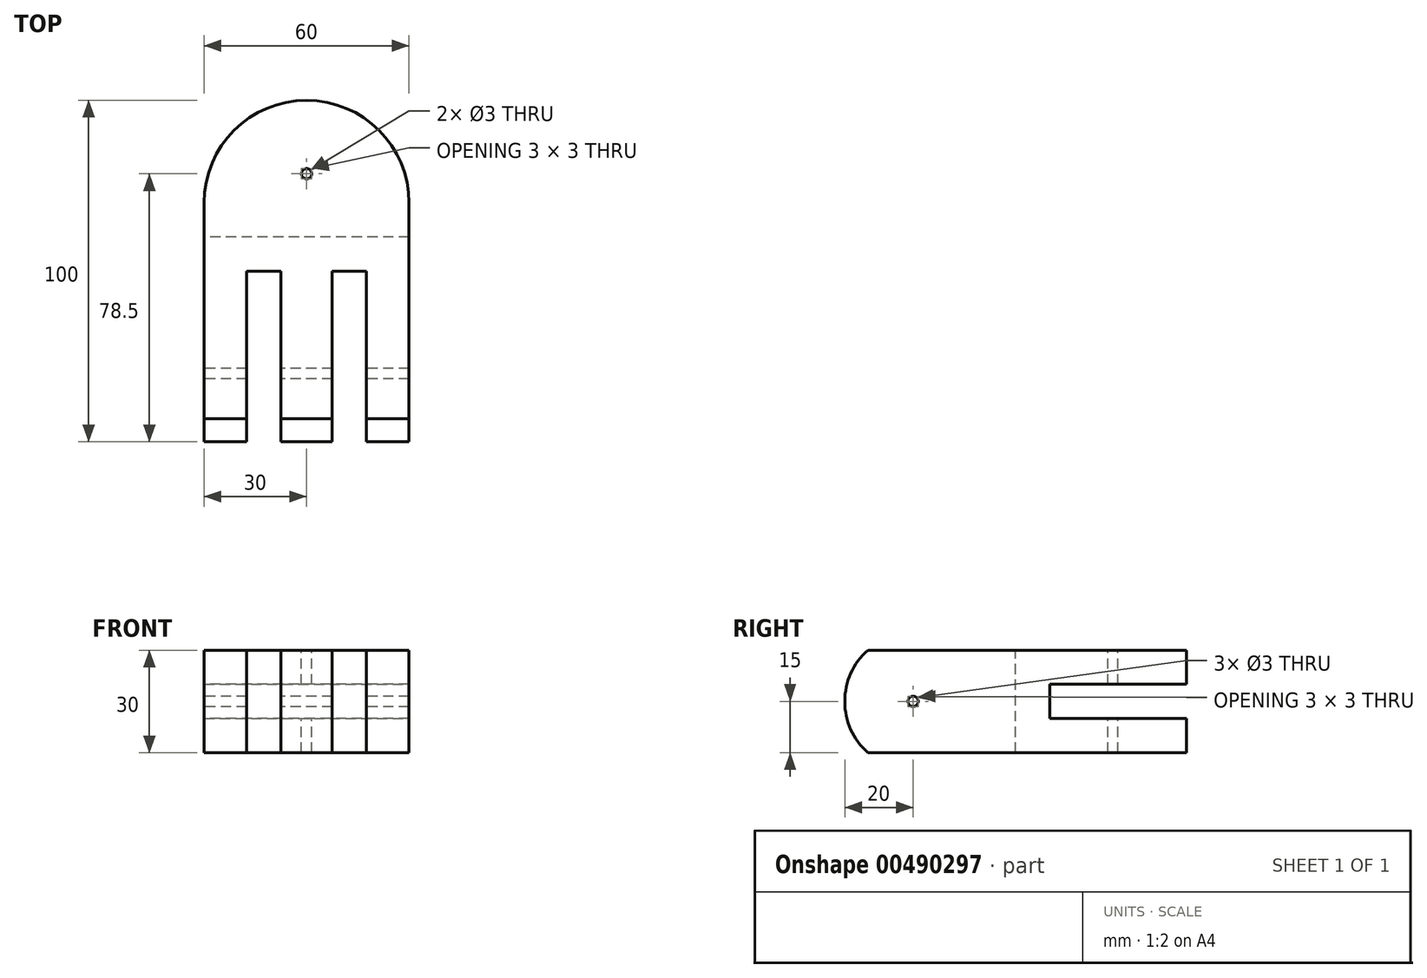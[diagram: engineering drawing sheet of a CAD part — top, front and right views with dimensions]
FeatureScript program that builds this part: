
annotation { "Feature Type Name" : "Feature", "Feature Type Description" : "" }
export const myFeature = defineFeature(function(context is Context, id is Id, definition is map)
    precondition{}
    {
        {
            var Q0;
            Q0=qCreatedBy(makeId("Top.planeOp"),FACE);
            var sketch = newSketch(context, id + "F0", { "sketchPlane" : qUnion([Q0])});
            skLineSegment(sketch, "E0.bottom", {"start": v(30, -50) * mm, "end": v(-30, -50) * mm});
            skLineSegment(sketch, "E0.top", {"start": v(30, 50) * mm, "end": v(-30, 50) * mm});
            skLineSegment(sketch, "E0.left", {"start": v(30, -50) * mm, "end": v(30, 50) * mm});
            skLineSegment(sketch, "E0.right", {"start": v(-30, -50) * mm, "end": v(-30, 50) * mm});
            skPoint(sketch, "E0.middle", {"position": v(0, 0) * mm});
            skSolve(sketch);
        }
        {
            var Q0;
            Q0 = qSketchRegion(id + "F0", true);
            extrude(context, id + "F1", {"entities" : qUnion([Q0]), "depth" : 40 * mm, "offsetDistance" : 25 * mm});
        }
        {
            var Q0;
            Q0=makeQuery(id+"F1.opExtrude","SWEPT_FACE",FACE,{"disambiguationData":[OSD([sQuery(id+"F0.wireOp",EDGE,"E0.top")])]});
            var sketch = newSketch(context, id + "F2", { "sketchPlane" : qUnion([Q0])});
            skLineSegment(sketch, "E1.left", {"start": v(-13, 40) * mm, "end": v(-13, 40) * mm});
            skLineSegment(sketch, "E2.bottom", {"start": v(-30, 25) * mm, "end": v(30, 25) * mm});
            skLineSegment(sketch, "E2.top", {"start": v(-30, 15) * mm, "end": v(30, 15) * mm});
            skLineSegment(sketch, "E2.left", {"start": v(-30, 25) * mm, "end": v(-30, 15) * mm});
            skLineSegment(sketch, "E2.right", {"start": v(30, 25) * mm, "end": v(30, 15) * mm});
            skSolve(sketch);
        }
        {
            var Q0;
            Q0=makeQuery(id+"F2.imprint","IMPRINT",FACE,{"disambiguationData":[TD([[makeQuery(id+"F2.imprint","IMPRINT",EDGE,{"derivedFrom":sQuery(id+"F2.wireOp",EDGE,"E2.bottom")}),-1.0]])]});
            extrude(context, id + "F3", {"entities" : qUnion([Q0]), "operationType" : NewBodyOperationType.REMOVE, "oppositeDirection" : true, "depth" : 40 * mm, "offsetDistance" : 25 * mm});
        }
        {
            var Q0;
            Q0=makeQuery(id+"F1.opExtrude","CAP_FACE",FACE,{"disambiguationData":[OSD([sQuery(id+"F0.wireOp",EDGE,"E0.bottom"),sQuery(id+"F0.wireOp",EDGE,"E0.top"),sQuery(id+"F0.wireOp",EDGE,"E0.left"),sQuery(id+"F0.wireOp",EDGE,"E0.right")])],"isStart":false});
            var sketch = newSketch(context, id + "F4", { "sketchPlane" : qUnion([Q0])});
            skCircle(sketch, "E3", {"center": v(0, 28.5) * mm, "radius": 1.5 * mm});
            skSolve(sketch);
        }
        {
            var Q0;
            Q0=makeQuery(id+"F4.imprint","IMPRINT",FACE,{"disambiguationData":[TD([[makeQuery(id+"F4.imprint","IMPRINT",EDGE,{"derivedFrom":sQuery(id+"F4.wireOp",EDGE,"E3")}),1.0]])]});
            extrude(context, id + "F5", {"entities" : qUnion([Q0]), "operationType" : NewBodyOperationType.REMOVE, "oppositeDirection" : true, "depth" : 88.4 * mm, "offsetDistance" : 25 * mm});
        }
        {
            var Q0;
            Q0=makeQuery(id+"F1.opExtrude","SWEPT_FACE",FACE,{"disambiguationData":[OSD([sQuery(id+"F0.wireOp",EDGE,"E0.right")])]});
            var sketch = newSketch(context, id + "F6", { "sketchPlane" : qUnion([Q0])});
            skCircle(sketch, "E4", {"center": v(30, 20) * mm, "radius": 1.5 * mm});
            skPoint(sketch, "E4.centerSnap0", {"position": v(-10, 20) * mm});
            skSolve(sketch);
        }
        {
            var Q0;
            Q0 = qSketchRegion(id + "F6", true);
            extrude(context, id + "F7", {"entities" : qUnion([Q0]), "operationType" : NewBodyOperationType.REMOVE, "oppositeDirection" : true, "depth" : 101.4 * mm, "offsetDistance" : 25 * mm});
        }
        {
            var Q0;
            Q0=makeQuery(id+"F1.opExtrude","CAP_FACE",FACE,{"disambiguationData":[OSD([sQuery(id+"F0.wireOp",EDGE,"E0.bottom"),sQuery(id+"F0.wireOp",EDGE,"E0.top"),sQuery(id+"F0.wireOp",EDGE,"E0.left"),sQuery(id+"F0.wireOp",EDGE,"E0.right")])],"isStart":false});
            var sketch = newSketch(context, id + "F8", { "sketchPlane" : qUnion([Q0])});
            skLineSegment(sketch, "E5.bottom", {"start": v(-17.5, -50) * mm, "end": v(-7.5, -50) * mm});
            skLineSegment(sketch, "E5.top", {"start": v(-17.5, 0) * mm, "end": v(-7.5, 0) * mm});
            skLineSegment(sketch, "E5.left", {"start": v(-17.5, -50) * mm, "end": v(-17.5, 0) * mm});
            skLineSegment(sketch, "E5.right", {"start": v(-7.5, -50) * mm, "end": v(-7.5, 0) * mm});
            skLineSegment(sketch, "E6.bottom", {"start": v(7.5, 0) * mm, "end": v(17.5, 0) * mm});
            skLineSegment(sketch, "E6.top", {"start": v(7.5, -50) * mm, "end": v(17.5, -50) * mm});
            skLineSegment(sketch, "E6.right", {"start": v(7.5, 0) * mm, "end": v(7.5, -50) * mm});
            skLineSegment(sketch, "E7", {"start": v(17.5, -50) * mm, "end": v(17.5, 0) * mm});
            skSolve(sketch);
        }
        {
            var Q0;
            Q0=makeQuery(id+"F8.imprint","IMPRINT",FACE,{"disambiguationData":[TD([[makeQuery(id+"F8.imprint","IMPRINT",EDGE,{"derivedFrom":sQuery(id+"F8.wireOp",EDGE,"E5.bottom")}),-1.0]])]});
            var Q1;
            Q1=makeQuery(id+"F8.imprint","IMPRINT",FACE,{"disambiguationData":[TD([[makeQuery(id+"F8.imprint","IMPRINT",EDGE,{"derivedFrom":sQuery(id+"F8.wireOp",EDGE,"AMtmPXIM-BORS-Hj5c-r4cM-iqdEoAU15gwC.bottom")}),-1.0]])]});
            var Q2;
            Q2=makeQuery(id+"F8.imprint","IMPRINT",FACE,{"disambiguationData":[TD([[makeQuery(id+"F8.imprint","IMPRINT",EDGE,{"derivedFrom":sQuery(id+"F8.wireOp",EDGE,"E6.bottom")}),-1.0]])]});
            extrude(context, id + "F9", {"entities" : qUnion([Q0, Q1, Q2]), "operationType" : NewBodyOperationType.REMOVE, "oppositeDirection" : true, "depth" : 70.3 * mm, "offsetDistance" : 25 * mm});
        }
        {
            var Q0;
            {var subQ0=sQuery(id+"F0.wireOp",EDGE,"E0.bottom");var subQ1=sQuery(id+"F0.wireOp",EDGE,"E0.right");Q0=makeQuery(id+"F9.boolean.opBoolean","SPLIT",EDGE,{"disambiguationData":[TD([makeQuery(id+"F1.opExtrude","SWEPT_FACE",FACE,{"disambiguationData":[OSD([subQ1])]})])],"derivedFrom":makeQuery(id+"F1.opExtrude","CAP_EDGE",EDGE,{"disambiguationData":[OSD([subQ0])],"isStart":true})});}
            var Q1;
            {var subQ0=sQuery(id+"F0.wireOp",EDGE,"E0.bottom");var subQ1=sQuery(id+"F0.wireOp",EDGE,"E0.right");Q1=makeQuery(id+"F9.boolean.opBoolean","SPLIT",EDGE,{"disambiguationData":[TD([makeQuery(id+"F1.opExtrude","SWEPT_FACE",FACE,{"disambiguationData":[OSD([subQ1])]})])],"derivedFrom":makeQuery(id+"F1.opExtrude","CAP_EDGE",EDGE,{"disambiguationData":[OSD([subQ0])],"isStart":false})});}
            var Q2;
            {var subQ0=sQuery(id+"F0.wireOp",EDGE,"E0.bottom");Q2=makeQuery(id+"F9.boolean.opBoolean","SPLIT",EDGE,{"disambiguationData":[TD([makeQuery(id+"F9.opExtrude","SWEPT_FACE",FACE,{"disambiguationData":[OSD([sQuery(id+"F8.wireOp",EDGE,"E5.right")])]})])],"derivedFrom":makeQuery(id+"F1.opExtrude","CAP_EDGE",EDGE,{"disambiguationData":[OSD([subQ0])],"isStart":false})});}
            var Q3;
            {var subQ0=sQuery(id+"F0.wireOp",EDGE,"E0.bottom");Q3=makeQuery(id+"F9.boolean.opBoolean","SPLIT",EDGE,{"disambiguationData":[TD([makeQuery(id+"F9.opExtrude","SWEPT_FACE",FACE,{"disambiguationData":[OSD([sQuery(id+"F8.wireOp",EDGE,"E5.right")])]})])],"derivedFrom":makeQuery(id+"F1.opExtrude","CAP_EDGE",EDGE,{"disambiguationData":[OSD([subQ0])],"isStart":true})});}
            var Q4;
            {var subQ0=sQuery(id+"F0.wireOp",EDGE,"E0.bottom");var subQ1=sQuery(id+"F0.wireOp",EDGE,"E0.left");Q4=makeQuery(id+"F9.boolean.opBoolean","SPLIT",EDGE,{"disambiguationData":[TD([makeQuery(id+"F1.opExtrude","SWEPT_FACE",FACE,{"disambiguationData":[OSD([subQ1])]})])],"derivedFrom":makeQuery(id+"F1.opExtrude","CAP_EDGE",EDGE,{"disambiguationData":[OSD([subQ0])],"isStart":true})});}
            var Q5;
            {var subQ0=sQuery(id+"F0.wireOp",EDGE,"E0.bottom");var subQ1=sQuery(id+"F0.wireOp",EDGE,"E0.left");Q5=makeQuery(id+"F9.boolean.opBoolean","SPLIT",EDGE,{"disambiguationData":[TD([makeQuery(id+"F1.opExtrude","SWEPT_FACE",FACE,{"disambiguationData":[OSD([subQ1])]})])],"derivedFrom":makeQuery(id+"F1.opExtrude","CAP_EDGE",EDGE,{"disambiguationData":[OSD([subQ0])],"isStart":false})});}
            fillet(context, id + "F10", {"entities" : qUnion([Q0, Q1, Q2, Q3, Q4, Q5]), "radius" : 20 * mm, "tangentPropagation" : true, "allowEdgeOverflow" : false});
        }
        {
            var Q0;
            {var subQ0=sQuery(id+"F0.wireOp",EDGE,"E0.right");var subQ1=sQuery(id+"F0.wireOp",EDGE,"E0.top");Q0=makeQuery(id+"F3.boolean.opBoolean","SPLIT",EDGE,{"disambiguationData":[TD([makeQuery(id+"F3.opExtrude","SWEPT_FACE",FACE,{"disambiguationData":[OSD([sQuery(id+"F2.wireOp",EDGE,"E2.bottom")])]})])],"derivedFrom":makeQuery(id+"F1.opExtrude","SWEPT_EDGE",EDGE,{"disambiguationData":[OSD([subQ1,subQ0])]})});}
            var Q1;
            {var subQ0=sQuery(id+"F0.wireOp",EDGE,"E0.right");var subQ1=sQuery(id+"F0.wireOp",EDGE,"E0.top");Q1=makeQuery(id+"F3.boolean.opBoolean","SPLIT",EDGE,{"disambiguationData":[TD([makeQuery(id+"F3.opExtrude","SWEPT_FACE",FACE,{"disambiguationData":[OSD([sQuery(id+"F2.wireOp",EDGE,"E2.top")])]})])],"derivedFrom":makeQuery(id+"F1.opExtrude","SWEPT_EDGE",EDGE,{"disambiguationData":[OSD([subQ1,subQ0])]})});}
            var Q2;
            {var subQ0=sQuery(id+"F0.wireOp",EDGE,"E0.left");var subQ1=sQuery(id+"F0.wireOp",EDGE,"E0.top");Q2=makeQuery(id+"F3.boolean.opBoolean","SPLIT",EDGE,{"disambiguationData":[TD([makeQuery(id+"F3.opExtrude","SWEPT_FACE",FACE,{"disambiguationData":[OSD([sQuery(id+"F2.wireOp",EDGE,"E2.bottom")])]})])],"derivedFrom":makeQuery(id+"F1.opExtrude","SWEPT_EDGE",EDGE,{"disambiguationData":[OSD([subQ1,subQ0])]})});}
            var Q3;
            {var subQ0=sQuery(id+"F0.wireOp",EDGE,"E0.left");var subQ1=sQuery(id+"F0.wireOp",EDGE,"E0.top");Q3=makeQuery(id+"F3.boolean.opBoolean","SPLIT",EDGE,{"disambiguationData":[TD([makeQuery(id+"F3.opExtrude","SWEPT_FACE",FACE,{"disambiguationData":[OSD([sQuery(id+"F2.wireOp",EDGE,"E2.top")])]})])],"derivedFrom":makeQuery(id+"F1.opExtrude","SWEPT_EDGE",EDGE,{"disambiguationData":[OSD([subQ1,subQ0])]})});}
            fillet(context, id + "F11", {"entities" : qUnion([Q0, Q1, Q2, Q3]), "radius" : 30 * mm, "tangentPropagation" : true, "allowEdgeOverflow" : false});
        }
        {
            var Q0;
            Q0=makeQuery(id+"F1.opExtrude","CAP_FACE",FACE,{"disambiguationData":[OSD([sQuery(id+"F0.wireOp",EDGE,"E0.bottom"),sQuery(id+"F0.wireOp",EDGE,"E0.top"),sQuery(id+"F0.wireOp",EDGE,"E0.left"),sQuery(id+"F0.wireOp",EDGE,"E0.right")])],"isStart":false});
            extrude(context, id + "F12", {"entities" : qUnion([Q0]), "operationType" : NewBodyOperationType.REMOVE, "oppositeDirection" : true, "depth" : 5 * mm, "offsetDistance" : 25 * mm});
        }
        {
            var Q0;
            Q0=makeQuery(id+"F1.opExtrude","CAP_FACE",FACE,{"disambiguationData":[OSD([sQuery(id+"F0.wireOp",EDGE,"E0.bottom"),sQuery(id+"F0.wireOp",EDGE,"E0.top"),sQuery(id+"F0.wireOp",EDGE,"E0.left"),sQuery(id+"F0.wireOp",EDGE,"E0.right")])],"isStart":true});
            extrude(context, id + "F13", {"entities" : qUnion([Q0]), "operationType" : NewBodyOperationType.REMOVE, "oppositeDirection" : true, "depth" : 5 * mm, "offsetDistance" : 25 * mm});
        }
        {
            var Q0;
            {var subQ0=sQuery(id+"F0.wireOp",EDGE,"E0.right");var subQ1=sQuery(id+"F0.wireOp",EDGE,"E0.left");var subQ2=sQuery(id+"F0.wireOp",EDGE,"E0.top");var subQ3=sQuery(id+"F0.wireOp",EDGE,"E0.bottom");var subQ4=makeQuery(id+"F1.opExtrude","CAP_FACE",FACE,{"disambiguationData":[OSD([subQ3,subQ2,subQ1,subQ0])],"isStart":true});Q0=makeQuery(id+"F13.boolean.opBoolean","COPY",FACE,{"derivedFrom":makeQuery(id+"F13.opExtrude","SWEPT_FACE",FACE,{"disambiguationData":[OSD([subQ3,subQ2,subQ1,subQ0]),TDD([makeQuery(id+"F10.opFillet","BLEND_EDGE",EDGE,{"blendedFrom":[makeQuery(id+"F9.boolean.opBoolean","SPLIT",EDGE,{"disambiguationData":[TD([makeQuery(id+"F1.opExtrude","SWEPT_FACE",FACE,{"disambiguationData":[OSD([subQ1])]})])],"derivedFrom":makeQuery(id+"F1.opExtrude","CAP_EDGE",EDGE,{"disambiguationData":[OSD([subQ3])],"isStart":true})}),subQ4],"blendedInto":[subQ4]})])]})});}
            var Q1;
            {var subQ0=sQuery(id+"F0.wireOp",EDGE,"E0.right");var subQ1=sQuery(id+"F0.wireOp",EDGE,"E0.left");var subQ2=sQuery(id+"F0.wireOp",EDGE,"E0.top");var subQ3=sQuery(id+"F0.wireOp",EDGE,"E0.bottom");var subQ4=makeQuery(id+"F1.opExtrude","CAP_FACE",FACE,{"disambiguationData":[OSD([subQ3,subQ2,subQ1,subQ0])],"isStart":true});Q1=makeQuery(id+"F13.boolean.opBoolean","COPY",FACE,{"derivedFrom":makeQuery(id+"F13.opExtrude","SWEPT_FACE",FACE,{"disambiguationData":[OSD([subQ3,subQ2,subQ1,subQ0]),TDD([makeQuery(id+"F10.opFillet","BLEND_EDGE",EDGE,{"blendedFrom":[makeQuery(id+"F9.boolean.opBoolean","SPLIT",EDGE,{"disambiguationData":[TD([makeQuery(id+"F9.opExtrude","SWEPT_FACE",FACE,{"disambiguationData":[OSD([sQuery(id+"F8.wireOp",EDGE,"E5.right")])]})])],"derivedFrom":makeQuery(id+"F1.opExtrude","CAP_EDGE",EDGE,{"disambiguationData":[OSD([subQ3])],"isStart":true})}),subQ4],"blendedInto":[subQ4]})])]})});}
            var Q2;
            {var subQ0=sQuery(id+"F0.wireOp",EDGE,"E0.right");var subQ1=sQuery(id+"F0.wireOp",EDGE,"E0.left");var subQ2=sQuery(id+"F0.wireOp",EDGE,"E0.top");var subQ3=sQuery(id+"F0.wireOp",EDGE,"E0.bottom");var subQ4=makeQuery(id+"F1.opExtrude","CAP_FACE",FACE,{"disambiguationData":[OSD([subQ3,subQ2,subQ1,subQ0])],"isStart":true});Q2=makeQuery(id+"F13.boolean.opBoolean","COPY",FACE,{"derivedFrom":makeQuery(id+"F13.opExtrude","SWEPT_FACE",FACE,{"disambiguationData":[OSD([subQ3,subQ2,subQ1,subQ0]),TDD([makeQuery(id+"F10.opFillet","BLEND_EDGE",EDGE,{"blendedFrom":[makeQuery(id+"F9.boolean.opBoolean","SPLIT",EDGE,{"disambiguationData":[TD([makeQuery(id+"F1.opExtrude","SWEPT_FACE",FACE,{"disambiguationData":[OSD([subQ0])]})])],"derivedFrom":makeQuery(id+"F1.opExtrude","CAP_EDGE",EDGE,{"disambiguationData":[OSD([subQ3])],"isStart":true})}),subQ4],"blendedInto":[subQ4]})])]})});}
            var Q3;
            {var subQ0=sQuery(id+"F0.wireOp",EDGE,"E0.right");var subQ1=sQuery(id+"F0.wireOp",EDGE,"E0.left");var subQ2=sQuery(id+"F0.wireOp",EDGE,"E0.top");var subQ3=sQuery(id+"F0.wireOp",EDGE,"E0.bottom");var subQ4=makeQuery(id+"F1.opExtrude","CAP_FACE",FACE,{"disambiguationData":[OSD([subQ3,subQ2,subQ1,subQ0])],"isStart":false});Q3=makeQuery(id+"F12.boolean.opBoolean","COPY",FACE,{"derivedFrom":makeQuery(id+"F12.opExtrude","SWEPT_FACE",FACE,{"disambiguationData":[OSD([subQ3,subQ2,subQ1,subQ0]),TDD([makeQuery(id+"F10.opFillet","BLEND_EDGE",EDGE,{"blendedFrom":[makeQuery(id+"F9.boolean.opBoolean","SPLIT",EDGE,{"disambiguationData":[TD([makeQuery(id+"F1.opExtrude","SWEPT_FACE",FACE,{"disambiguationData":[OSD([subQ1])]})])],"derivedFrom":makeQuery(id+"F1.opExtrude","CAP_EDGE",EDGE,{"disambiguationData":[OSD([subQ3])],"isStart":false})}),subQ4],"blendedInto":[subQ4]})])]})});}
            var Q4;
            {var subQ0=sQuery(id+"F0.wireOp",EDGE,"E0.right");var subQ1=sQuery(id+"F0.wireOp",EDGE,"E0.left");var subQ2=sQuery(id+"F0.wireOp",EDGE,"E0.top");var subQ3=sQuery(id+"F0.wireOp",EDGE,"E0.bottom");var subQ4=makeQuery(id+"F1.opExtrude","CAP_FACE",FACE,{"disambiguationData":[OSD([subQ3,subQ2,subQ1,subQ0])],"isStart":false});Q4=makeQuery(id+"F12.boolean.opBoolean","COPY",FACE,{"derivedFrom":makeQuery(id+"F12.opExtrude","SWEPT_FACE",FACE,{"disambiguationData":[OSD([subQ3,subQ2,subQ1,subQ0]),TDD([makeQuery(id+"F10.opFillet","BLEND_EDGE",EDGE,{"blendedFrom":[makeQuery(id+"F9.boolean.opBoolean","SPLIT",EDGE,{"disambiguationData":[TD([makeQuery(id+"F9.opExtrude","SWEPT_FACE",FACE,{"disambiguationData":[OSD([sQuery(id+"F8.wireOp",EDGE,"E5.right")])]})])],"derivedFrom":makeQuery(id+"F1.opExtrude","CAP_EDGE",EDGE,{"disambiguationData":[OSD([subQ3])],"isStart":false})}),subQ4],"blendedInto":[subQ4]})])]})});}
            var Q5;
            {var subQ0=sQuery(id+"F0.wireOp",EDGE,"E0.right");var subQ1=sQuery(id+"F0.wireOp",EDGE,"E0.left");var subQ2=sQuery(id+"F0.wireOp",EDGE,"E0.top");var subQ3=sQuery(id+"F0.wireOp",EDGE,"E0.bottom");var subQ4=makeQuery(id+"F1.opExtrude","CAP_FACE",FACE,{"disambiguationData":[OSD([subQ3,subQ2,subQ1,subQ0])],"isStart":false});Q5=makeQuery(id+"F12.boolean.opBoolean","COPY",FACE,{"derivedFrom":makeQuery(id+"F12.opExtrude","SWEPT_FACE",FACE,{"disambiguationData":[OSD([subQ3,subQ2,subQ1,subQ0]),TDD([makeQuery(id+"F10.opFillet","BLEND_EDGE",EDGE,{"blendedFrom":[makeQuery(id+"F9.boolean.opBoolean","SPLIT",EDGE,{"disambiguationData":[TD([makeQuery(id+"F1.opExtrude","SWEPT_FACE",FACE,{"disambiguationData":[OSD([subQ0])]})])],"derivedFrom":makeQuery(id+"F1.opExtrude","CAP_EDGE",EDGE,{"disambiguationData":[OSD([subQ3])],"isStart":false})}),subQ4],"blendedInto":[subQ4]})])]})});}
            extrude(context, id + "F14", {"entities" : qUnion([Q0, Q1, Q2, Q3, Q4, Q5]), "operationType" : NewBodyOperationType.REMOVE, "oppositeDirection" : true, "depth" : 25 * mm, "offsetDistance" : 25 * mm});
        }
    });
